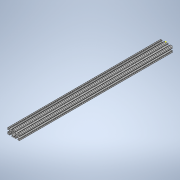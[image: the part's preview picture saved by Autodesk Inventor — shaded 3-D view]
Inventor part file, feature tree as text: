
AUTODESK INVENTOR PART (.ipt)
format: ipt  version: 2020 (Build 240168000, 168)  size: 334,848 bytes
history: native  units: in
note: dims shown in document units (in); Inventor stores cm internally (conversion verified against a paired STEP export)
features: sketch x2, extrude x1
ambient origin geometry x8: Origin, YZ Plane, XZ Plane, XY Plane, X Axis, Y Axis, Z Axis, Center Point
bodies: Solid1 (feature_tree)
feature tree (3):
  extrude  "Extrusion1"  [1 undecoded]
  sketch  "Sketch2"
  sketch  "Sketch1"  dims[d0=25.0in d1=0.0in]
note: 1 required parameter value undecoded (feature->parameter linkage not recoverable at this tier; creation-order binding heuristic only, values carry confidence <= 0.55)
